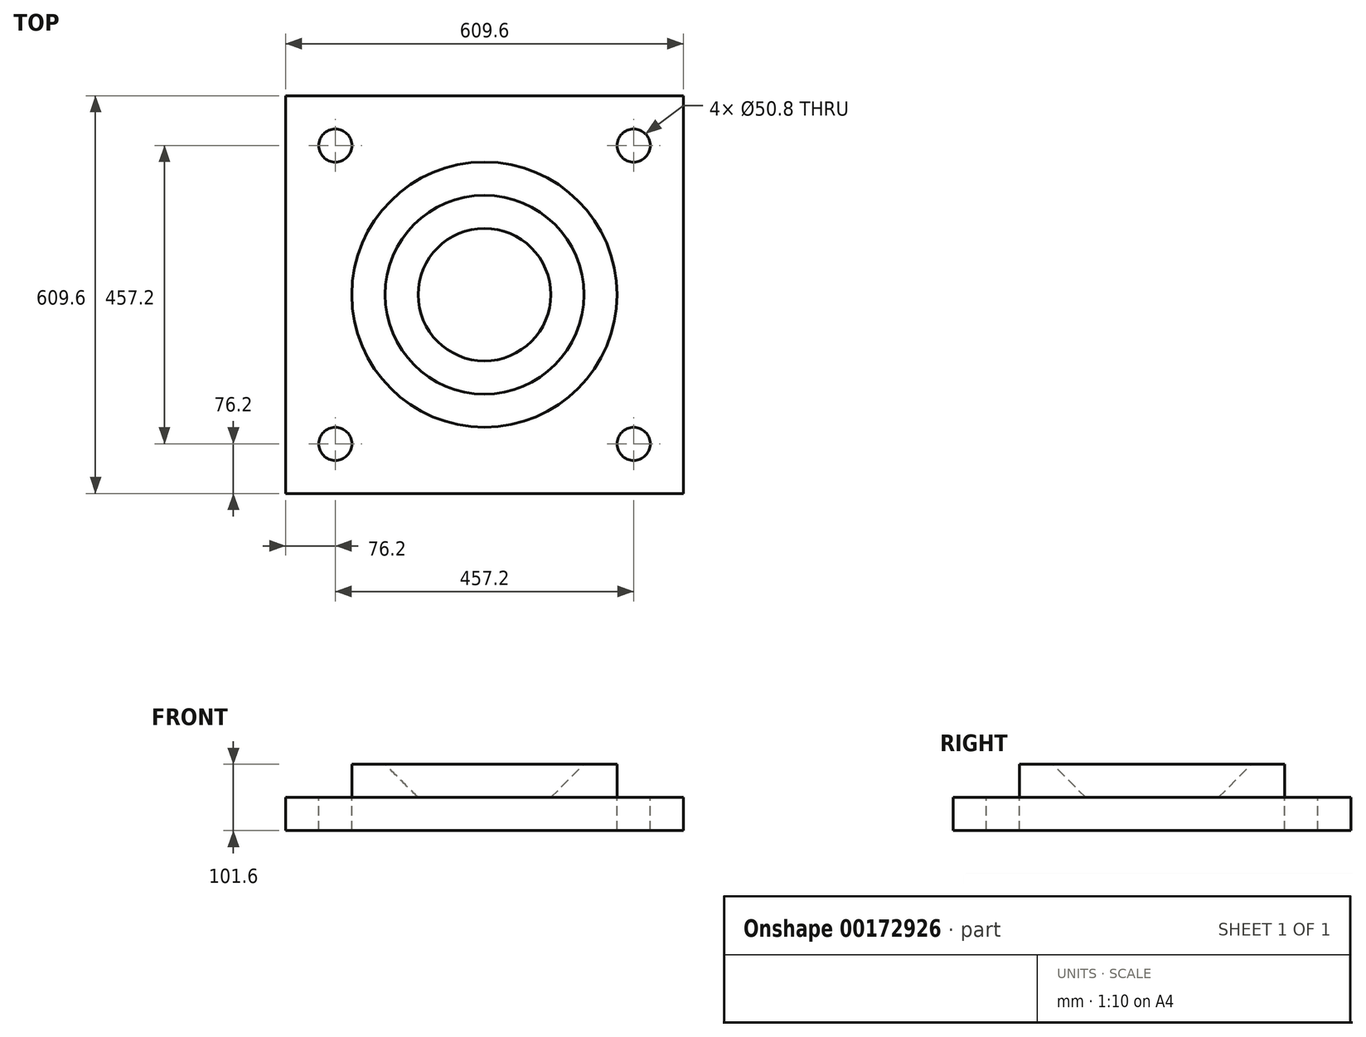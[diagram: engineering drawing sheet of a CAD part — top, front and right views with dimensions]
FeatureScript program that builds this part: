
annotation { "Feature Type Name" : "Feature", "Feature Type Description" : "" }
export const myFeature = defineFeature(function(context is Context, id is Id, definition is map)
    precondition{}
    {
        {
            var Q0;
            Q0=qCreatedBy(makeId("Top.planeOp"),FACE);
            var sketch = newSketch(context, id + "F0", { "sketchPlane" : qUnion([Q0])});
            skLineSegment(sketch, "E0.bottom", {"start": v(304.8, -304.8) * mm, "end": v(-304.8, -304.8) * mm});
            skLineSegment(sketch, "E0.top", {"start": v(304.8, 304.8) * mm, "end": v(-304.8, 304.8) * mm});
            skLineSegment(sketch, "E0.left", {"start": v(304.8, -304.8) * mm, "end": v(304.8, 304.8) * mm});
            skLineSegment(sketch, "E0.right", {"start": v(-304.8, -304.8) * mm, "end": v(-304.8, 304.8) * mm});
            skPoint(sketch, "E0.middle", {"position": v(0, 0) * mm});
            skSolve(sketch);
        }
        {
            var Q0;
            Q0=makeQuery(id+"F0.imprint","IMPRINT",FACE,{"disambiguationData":[TD([[makeQuery(id+"F0.imprint","IMPRINT",EDGE,{"derivedFrom":sQuery(id+"F0.wireOp",EDGE,"E0.bottom")}),-1.0]])]});
            extrude(context, id + "F1", {"entities" : qUnion([Q0]), "depth" : 50.8 * mm});
        }
        {
            var Q0;
            Q0=qCreatedBy(makeId("Front.planeOp"),FACE);
            var sketch = newSketch(context, id + "F2", { "sketchPlane" : qUnion([Q0])});
            skLineSegment(sketch, "E1", {"start": v(0, 0) * mm, "end": v(0, 50.8) * mm, "construction": true});
            skLineSegment(sketch, "E2", {"start": v(101.6, 50.8) * mm, "end": v(152.4, 101.6) * mm});
            skLineSegment(sketch, "E3", {"start": v(152.4, 101.6) * mm, "end": v(203.2, 101.6) * mm});
            skLineSegment(sketch, "E4", {"start": v(203.2, 101.6) * mm, "end": v(203.2, 50.8) * mm});
            skLineSegment(sketch, "E5", {"start": v(203.2, 50.8) * mm, "end": v(101.6, 50.8) * mm});
            skSolve(sketch);
        }
        {
            var Q0;
            Q0=makeQuery(id+"F2.imprint","IMPRINT",FACE,{"disambiguationData":[TD([[makeQuery(id+"F2.imprint","IMPRINT",EDGE,{"derivedFrom":sQuery(id+"F2.wireOp",EDGE,"E2")}),-1.0]])]});
            var Q1;
            Q1=sQuery(id+"F2.wireOp",EDGE,"E1");
            revolve(context, id + "F3", {"operationType" : NewBodyOperationType.ADD, "entities" : qUnion([Q0]), "axis" : qUnion([Q1]), "revolveType" : RevolveType.FULL});
        }
        {
            var Q0;
            {var subQ0=sQuery(id+"F0.wireOp",EDGE,"E0.right");var subQ1=sQuery(id+"F0.wireOp",EDGE,"E0.left");var subQ2=sQuery(id+"F0.wireOp",EDGE,"E0.top");var subQ3=sQuery(id+"F0.wireOp",EDGE,"E0.bottom");Q0=makeQuery(id+"F3.boolean.opBoolean","SPLIT",FACE,{"disambiguationData":[TD([makeQuery(id+"F1.opExtrude","SWEPT_FACE",FACE,{"disambiguationData":[OSD([subQ3])]})])],"derivedFrom":makeQuery(id+"F1.opExtrude","CAP_FACE",FACE,{"disambiguationData":[OSD([subQ3,subQ2,subQ1,subQ0])],"isStart":false})});}
            var sketch = newSketch(context, id + "F4", { "sketchPlane" : qUnion([Q0])});
            skCircle(sketch, "E6", {"center": v(-228.6, 228.6) * mm, "radius": 25.4 * mm});
            skCircle(sketch, "E7", {"center": v(228.6, 228.6) * mm, "radius": 25.4 * mm});
            skCircle(sketch, "E8", {"center": v(228.6, -228.6) * mm, "radius": 25.4 * mm});
            skCircle(sketch, "E9", {"center": v(-228.6, -228.6) * mm, "radius": 25.4 * mm});
            skLineSegment(sketch, "E10.bottom", {"start": v(228.6, -228.6) * mm, "end": v(-228.6, -228.6) * mm, "construction": true});
            skLineSegment(sketch, "E10.top", {"start": v(228.6, 228.6) * mm, "end": v(-228.6, 228.6) * mm, "construction": true});
            skLineSegment(sketch, "E10.left", {"start": v(228.6, -228.6) * mm, "end": v(228.6, 228.6) * mm, "construction": true});
            skLineSegment(sketch, "E10.right", {"start": v(-228.6, -228.6) * mm, "end": v(-228.6, 228.6) * mm, "construction": true});
            skPoint(sketch, "E10.middle", {"position": v(0, 0) * mm});
            skSolve(sketch);
        }
        {
            var Q0;
            Q0 = qSketchRegion(id + "F4", true);
            extrude(context, id + "F5", {"entities" : qUnion([Q0]), "operationType" : NewBodyOperationType.REMOVE, "endBound" : BoundingType.THROUGH_ALL, "oppositeDirection" : true, "depth" : 25.4 * mm});
        }
    });
